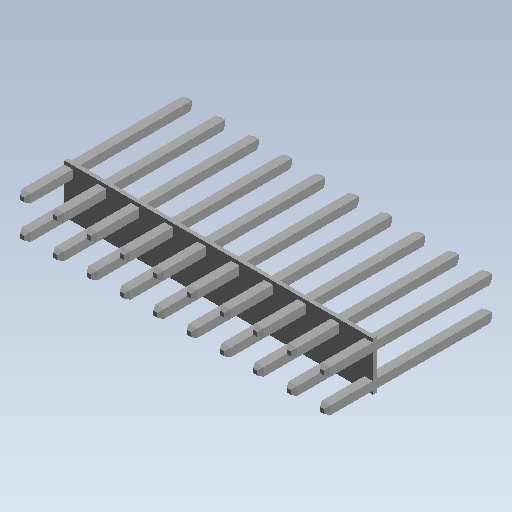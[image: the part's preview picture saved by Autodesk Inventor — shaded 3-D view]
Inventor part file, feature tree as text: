
AUTODESK INVENTOR PART (.ipt)
format: ipt  version: 2021 (Build 250183000, 183)  size: 565,248 bytes
history: native  units: mm (DEFAULTED — no unit token found)
features: other x7, extrude x2, sketch x2
ambient origin geometry x8: Origin, YZ Plane, XZ Plane, XY Plane, X Axis, Y Axis, Z Axis, Center Point
bodies: Solid1 (feature_tree)
feature tree (11):
  extrude  "Extrusion1"  Depth=18.507964mm TaperAngle=0.0deg
  extrude  "Extrusion2"  [1 undecoded]
  other  "0_XY"
  other  "0_YZ"
  other  "0_ZX"
  other  "0_X"
  other  "0_Y"
  other  "0_Z"
  other  "0_Center"
  sketch  "Sketch_2"
  sketch  "Sketch_1"  dims[d0=18.507964mm d1=0.0mm d2=15.24mm d3=0.0mm]
note: 1 required parameter value undecoded (feature->parameter linkage not recoverable at this tier; creation-order binding heuristic only, values carry confidence <= 0.55)
